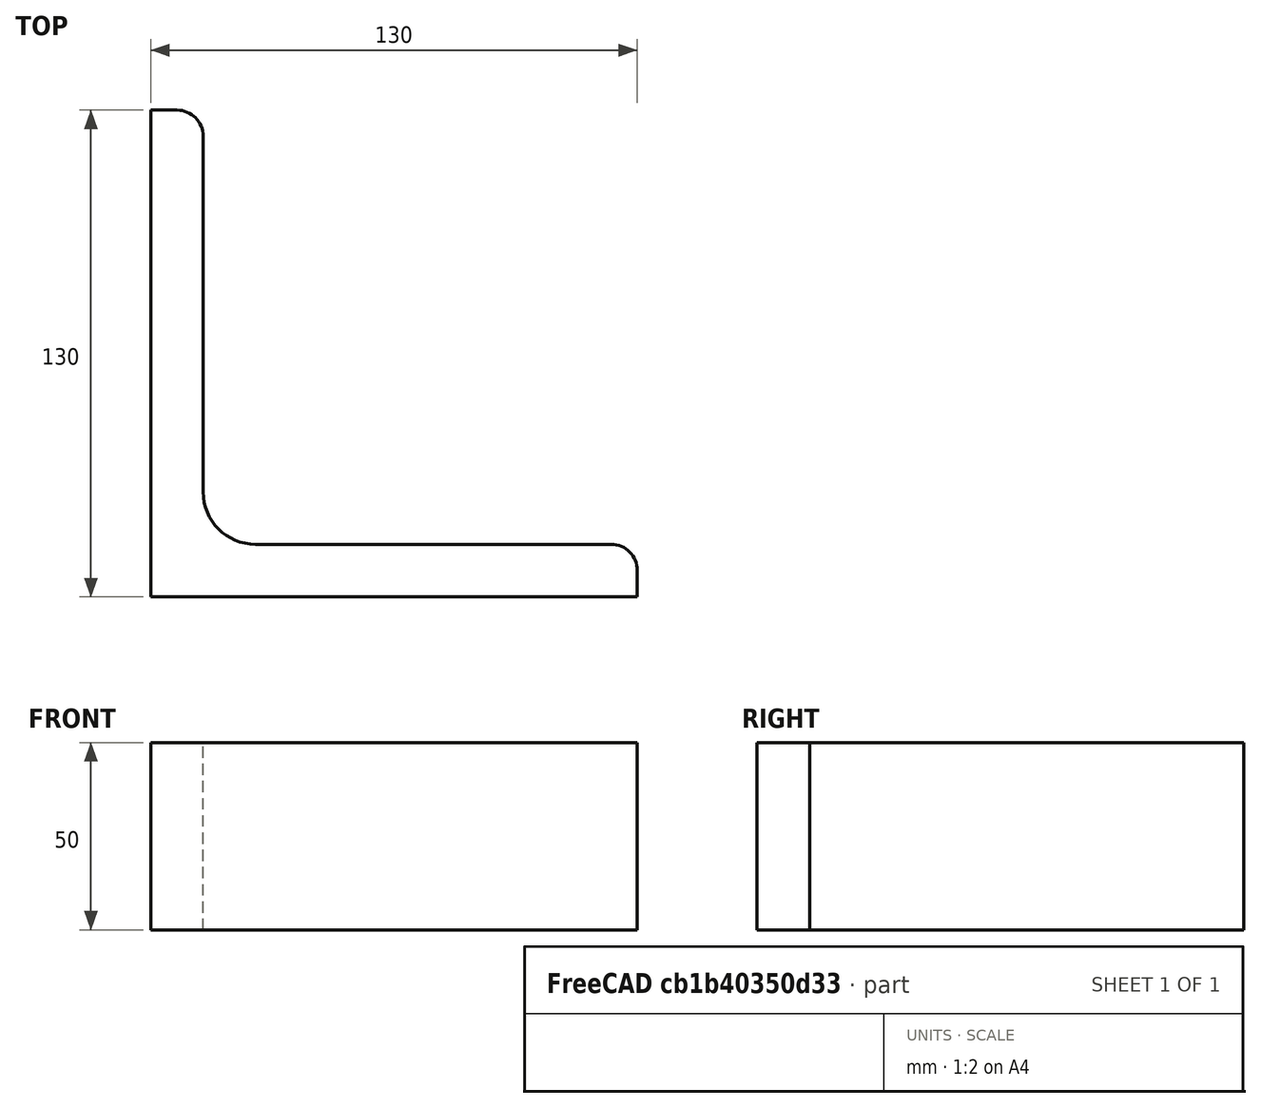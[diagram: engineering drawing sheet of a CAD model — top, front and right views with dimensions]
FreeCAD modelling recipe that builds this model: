
FCSTD DOCUMENT  (FreeCAD 0.15R4671 (Git))
Label: Angle Bar L130x130x14 EN10056 S235JR
License: All rights reserved
LicenseURL: http://en.wikipedia.org/wiki/All_rights_reserved
objects: Sketcher::SketchObject×1, Part::Extrusion×1
note: 2 computed .brp shape members not serialized (recipe doc carries the construction recipe); baked Part::Feature solids carry a one-line shape summary decoded from their .brp

FEATURE [Sketcher::SketchObject] Sketch
  sketch-geometry (9):
    g0: LineSegment StartX=0 StartY=0 StartZ=0 EndX=130 EndY=0 EndZ=0
    g1: LineSegment StartX=130 StartY=0 StartZ=0 EndX=130 EndY=7 EndZ=0
    g2: LineSegment StartX=123 StartY=14 StartZ=0 EndX=28 EndY=14 EndZ=0
    g3: LineSegment StartX=0 StartY=0 StartZ=0 EndX=0 EndY=130 EndZ=0
    g4: LineSegment StartX=0 StartY=130 StartZ=0 EndX=7 EndY=130 EndZ=0
    g5: LineSegment StartX=14 StartY=123 StartZ=0 EndX=14 EndY=28 EndZ=0
    g6: ArcOfCircle CenterX=28 CenterY=28 CenterZ=0 NormalX=0 NormalY=0 NormalZ=1 Radius=14 StartAngle=3.14159 EndAngle=4.71239
    g7: ArcOfCircle CenterX=7 CenterY=123 CenterZ=0 NormalX=0 NormalY=0 NormalZ=1 Radius=7 StartAngle=0 EndAngle=1.5708
    g8: ArcOfCircle CenterX=123 CenterY=7 CenterZ=0 NormalX=0 NormalY=0 NormalZ=1 Radius=7 StartAngle=0 EndAngle=1.5708
  constraints (23):
    c: Coincident(g0,g-1)
    c: Horizontal(g0)
    c: Coincident(g1,g0)
    c: Vertical(g1)
    c: Horizontal(g2)
    c: Coincident(g3,g-1)
    c: Vertical(g3)
    c: Coincident(g4,g3)
    c: Horizontal(g4)
    c: Vertical(g5)
    c: Tangent(g5,g6) = -1.5708
    c: Tangent(g2,g6) = 1.5708
    c: Tangent(g4,g7) = 1.5708
    c: Tangent(g5,g7) = 1.5708
    c: Tangent(g2,g8) = -1.5708
    c: Tangent(g1,g8) = -1.5708
    c: DistanceX(g0) = 130
    c: DistanceY(g3) = 130
    c: DistanceY(g0,g2) = 14
    c: DistanceX(g3,g5) = 14
    c: Radius(g6) = 14
    c: Radius(g8) = 7
    c: Radius(g7) = 7
FEATURE [Part::Extrusion] Extrude  label="Angle Bar L130x130x14 EN10056 S235JR"
  Base = -> Sketch
  Dir = (0,0,50)
  Solid = true
